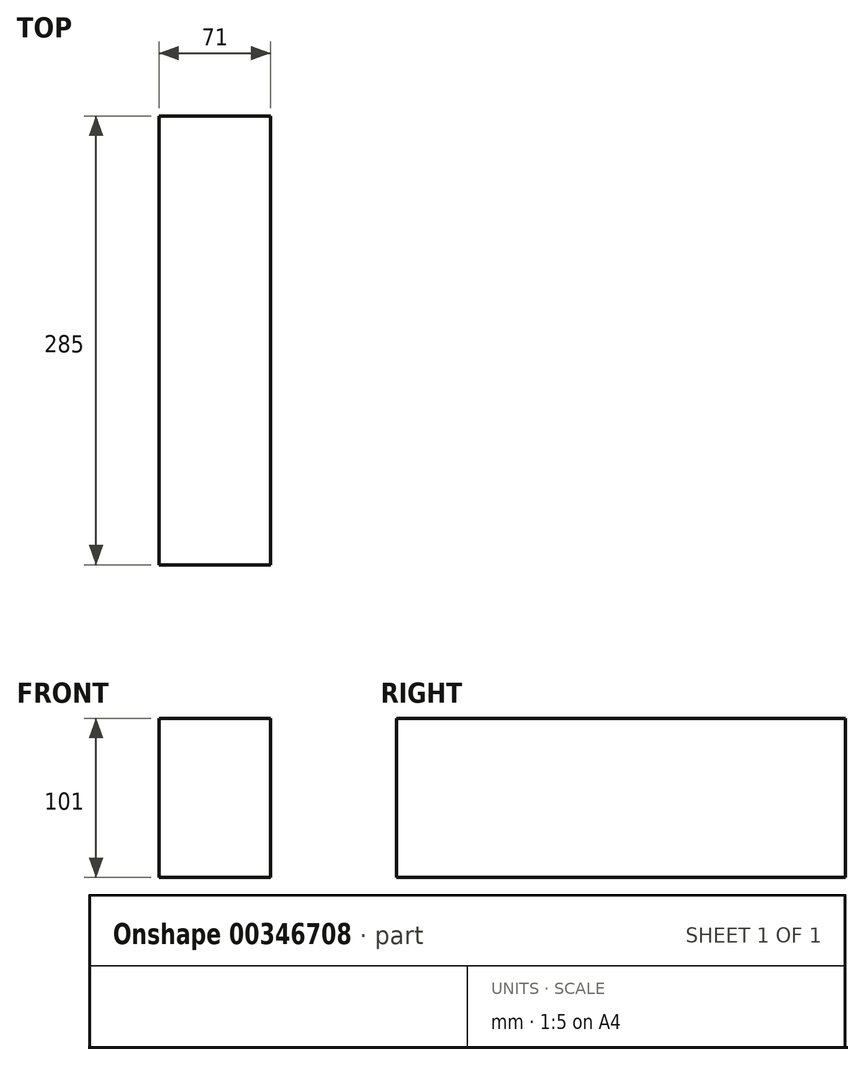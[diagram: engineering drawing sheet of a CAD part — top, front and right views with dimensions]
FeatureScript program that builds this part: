
annotation { "Feature Type Name" : "Feature", "Feature Type Description" : "" }
export const myFeature = defineFeature(function(context is Context, id is Id, definition is map)
    precondition{}
    {
        {
            var Q0;
            Q0=qCreatedBy(makeId("Front.planeOp"),FACE);
            var sketch = newSketch(context, id + "F0", { "sketchPlane" : qUnion([Q0])});
            skLineSegment(sketch, "E0.bottom", {"start": v(35.5, -50.5) * mm, "end": v(-35.5, -50.5) * mm});
            skLineSegment(sketch, "E0.top", {"start": v(35.5, 50.5) * mm, "end": v(-35.5, 50.5) * mm});
            skLineSegment(sketch, "E0.left", {"start": v(35.5, -50.5) * mm, "end": v(35.5, 50.5) * mm});
            skLineSegment(sketch, "E0.right", {"start": v(-35.5, -50.5) * mm, "end": v(-35.5, 50.5) * mm});
            skPoint(sketch, "E0.middle", {"position": v(0, 0) * mm});
            skSolve(sketch);
        }
        {
            var Q0;
            Q0 = qSketchRegion(id + "F0", true);
            var Q1;
            Q1=sQuery(id+"F0.wireOp",EDGE,"E0.top");
            var Q2;
            Q2=sQuery(id+"F0.wireOp",EDGE,"E0.left");
            var Q3;
            Q3=sQuery(id+"F0.wireOp",EDGE,"E0.bottom");
            var Q4;
            Q4=sQuery(id+"F0.wireOp",EDGE,"E0.right");
            extrude(context, id + "F1", {"entities" : qUnion([Q0]), "bodyType" : ToolBodyType.SURFACE, "surfaceEntities" : qUnion([Q1, Q2, Q3, Q4]), "depth" : 285 * mm});
        }
    });
